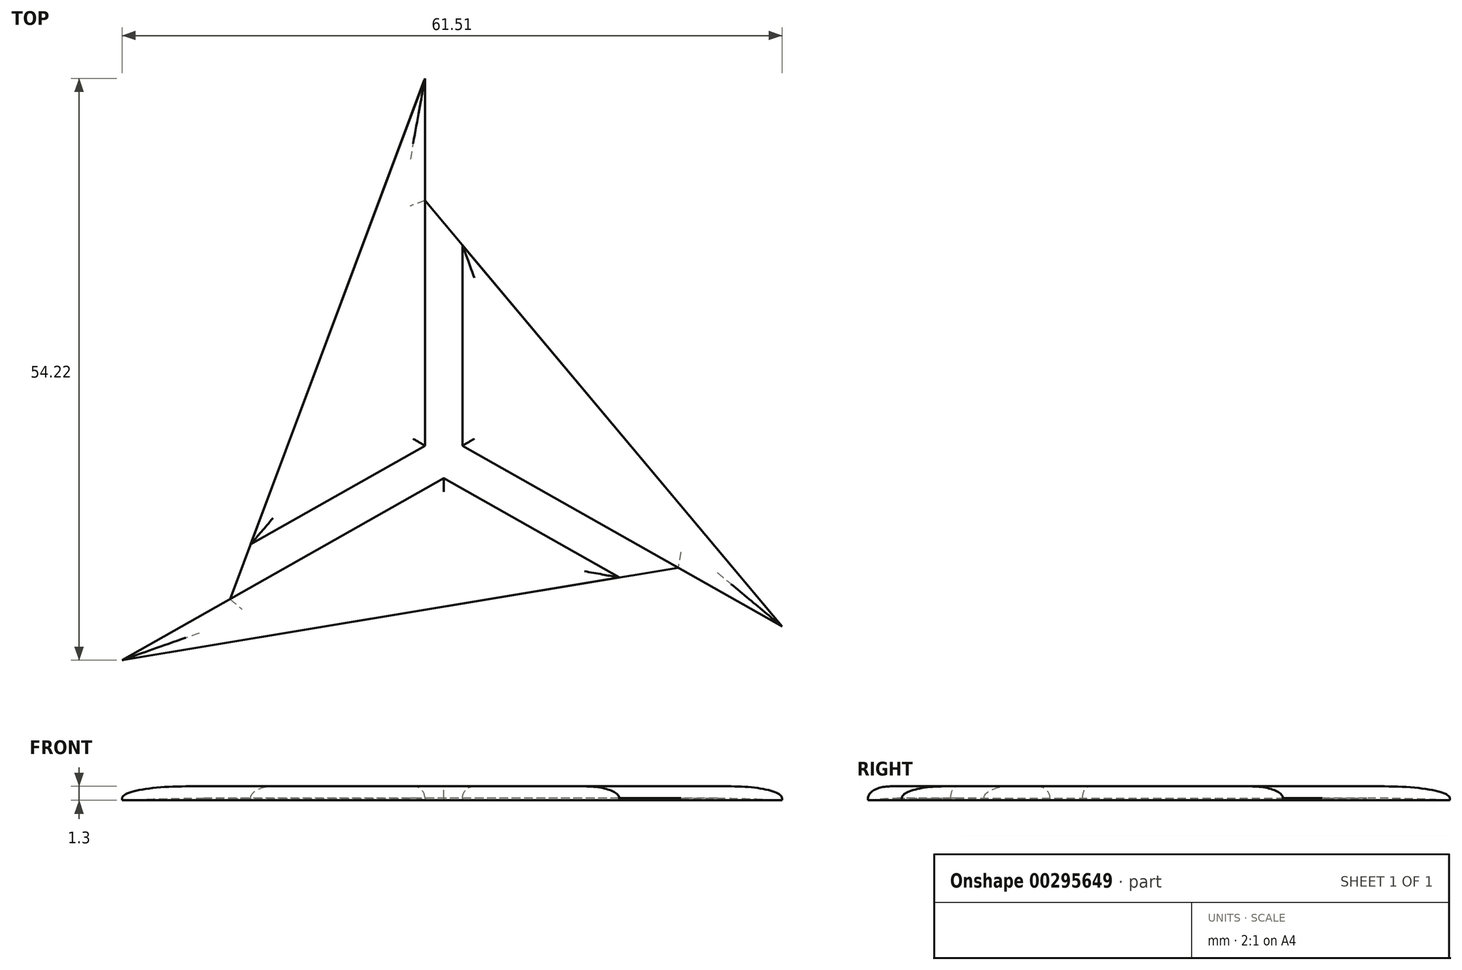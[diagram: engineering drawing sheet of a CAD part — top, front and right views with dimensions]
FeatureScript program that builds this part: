
annotation { "Feature Type Name" : "Feature", "Feature Type Description" : "" }
export const myFeature = defineFeature(function(context is Context, id is Id, definition is map)
    precondition{}
    {
        {
            var Q0;
            Q0=qCreatedBy(makeId("Top.planeOp"),FACE);
            var sketch = newSketch(context, id + "F0", { "sketchPlane" : qUnion([Q0])});
            skLineSegment(sketch, "E0.0", {"start": v(-40.27, 11.94) * mm, "end": v(-24.02, 55.35) * mm});
            skLineSegment(sketch, "E0.1", {"start": v(-24.02, 21.13) * mm, "end": v(-40.27, 11.94) * mm});
            skLineSegment(sketch, "E0.2", {"start": v(-24.02, 55.35) * mm, "end": v(-24.02, 21.13) * mm});
            skLineSegment(sketch, "E1.0", {"start": v(-20.52, 39.8) * mm, "end": v(9.26, 4.28) * mm});
            skLineSegment(sketch, "E1.1", {"start": v(-20.52, 21.13) * mm, "end": v(-20.52, 39.8) * mm});
            skLineSegment(sketch, "E1.2", {"start": v(9.26, 4.28) * mm, "end": v(-20.52, 21.13) * mm});
            skLineSegment(sketch, "E2.0", {"start": v(-5.92, 8.85) * mm, "end": v(-52.25, 1.13) * mm});
            skLineSegment(sketch, "E2.1", {"start": v(-22.27, 18.1) * mm, "end": v(-5.92, 8.85) * mm});
            skLineSegment(sketch, "E2.2", {"start": v(-52.25, 1.13) * mm, "end": v(-22.27, 18.1) * mm});
            skSolve(sketch);
        }
        {
            var Q0;
            Q0=qSketchRegion(id+"F0",true);
            extrude(context, id + "F1", {"entities" : qUnion([Q0]), "depth" : 1.3 * mm, "offsetDistance" : 25 * mm});
        }
        {
            var Q0;
            Q0=makeQuery(id+"F1.opExtrude","CAP_FACE",FACE,{"disambiguationData":[OSD([sQuery(id+"F0.wireOp",EDGE,"E0.0"),sQuery(id+"F0.wireOp",EDGE,"E0.1"),sQuery(id+"F0.wireOp",EDGE,"E0.2")])],"isStart":false});
            var Q1;
            Q1=makeQuery(id+"F1.opExtrude","CAP_FACE",FACE,{"disambiguationData":[OSD([sQuery(id+"F0.wireOp",EDGE,"E1.0"),sQuery(id+"F0.wireOp",EDGE,"E1.1"),sQuery(id+"F0.wireOp",EDGE,"E1.2")])],"isStart":false});
            var Q2;
            Q2=makeQuery(id+"F1.opExtrude","CAP_FACE",FACE,{"disambiguationData":[OSD([sQuery(id+"F0.wireOp",EDGE,"E2.0"),sQuery(id+"F0.wireOp",EDGE,"E2.1"),sQuery(id+"F0.wireOp",EDGE,"E2.2")])],"isStart":false});
            fillet(context, id + "F2", {"entities" : qUnion([Q0, Q1, Q2]), "radius" : 1.1 * mm, "tangentPropagation" : true, "allowEdgeOverflow" : false});
        }
        {
            var Q0;
            Q0=makeQuery(id+"F1.opExtrude","CAP_FACE",FACE,{"disambiguationData":[OSD([sQuery(id+"F0.wireOp",EDGE,"E1.0"),sQuery(id+"F0.wireOp",EDGE,"E1.1"),sQuery(id+"F0.wireOp",EDGE,"E1.2")])],"isStart":true});
            var sketch = newSketch(context, id + "F3", { "sketchPlane" : qUnion([Q0])});
            skLineSegment(sketch, "E3", {"start": v(9.26, -4.28) * mm, "end": v(-20.52, -39.8) * mm});
            skLineSegment(sketch, "E4", {"start": v(-20.52, -39.8) * mm, "end": v(-24.02, -43.97) * mm});
            skLineSegment(sketch, "E5", {"start": v(-24.02, -43.97) * mm, "end": v(-24.02, -55.35) * mm});
            skLineSegment(sketch, "E6", {"start": v(-24.02, -55.35) * mm, "end": v(-42.18, -6.82) * mm});
            skLineSegment(sketch, "E7", {"start": v(-42.18, -6.82) * mm, "end": v(-52.25, -1.13) * mm});
            skLineSegment(sketch, "E8", {"start": v(-52.25, -1.13) * mm, "end": v(-0.44, -9.76) * mm});
            skLineSegment(sketch, "E9", {"start": v(-0.44, -9.76) * mm, "end": v(9.26, -4.28) * mm});
            skSolve(sketch);
        }
        {
            var Q0;
            Q0=qSketchRegion(id+"F3",true);
            extrude(context, id + "F4", {"entities" : qUnion([Q0]), "oppositeDirection" : true, "depth" : 0.2 * mm, "offsetDistance" : 25 * mm});
        }
        {
            var Q0;
            Q0=makeQuery(id+"F4.opExtrude","CAP_FACE",FACE,{"disambiguationData":[OSD([sQuery(id+"F3.wireOp",EDGE,"E3"),sQuery(id+"F3.wireOp",EDGE,"E4"),sQuery(id+"F3.wireOp",EDGE,"E5"),sQuery(id+"F3.wireOp",EDGE,"E6"),sQuery(id+"F3.wireOp",EDGE,"E7"),sQuery(id+"F3.wireOp",EDGE,"E8"),sQuery(id+"F3.wireOp",EDGE,"E9")])],"isStart":false});
            fillet(context, id + "F5", {"entities" : qUnion([Q0]), "radius" : 5 * mm, "tangentPropagation" : true, "allowEdgeOverflow" : false});
        }
    });
